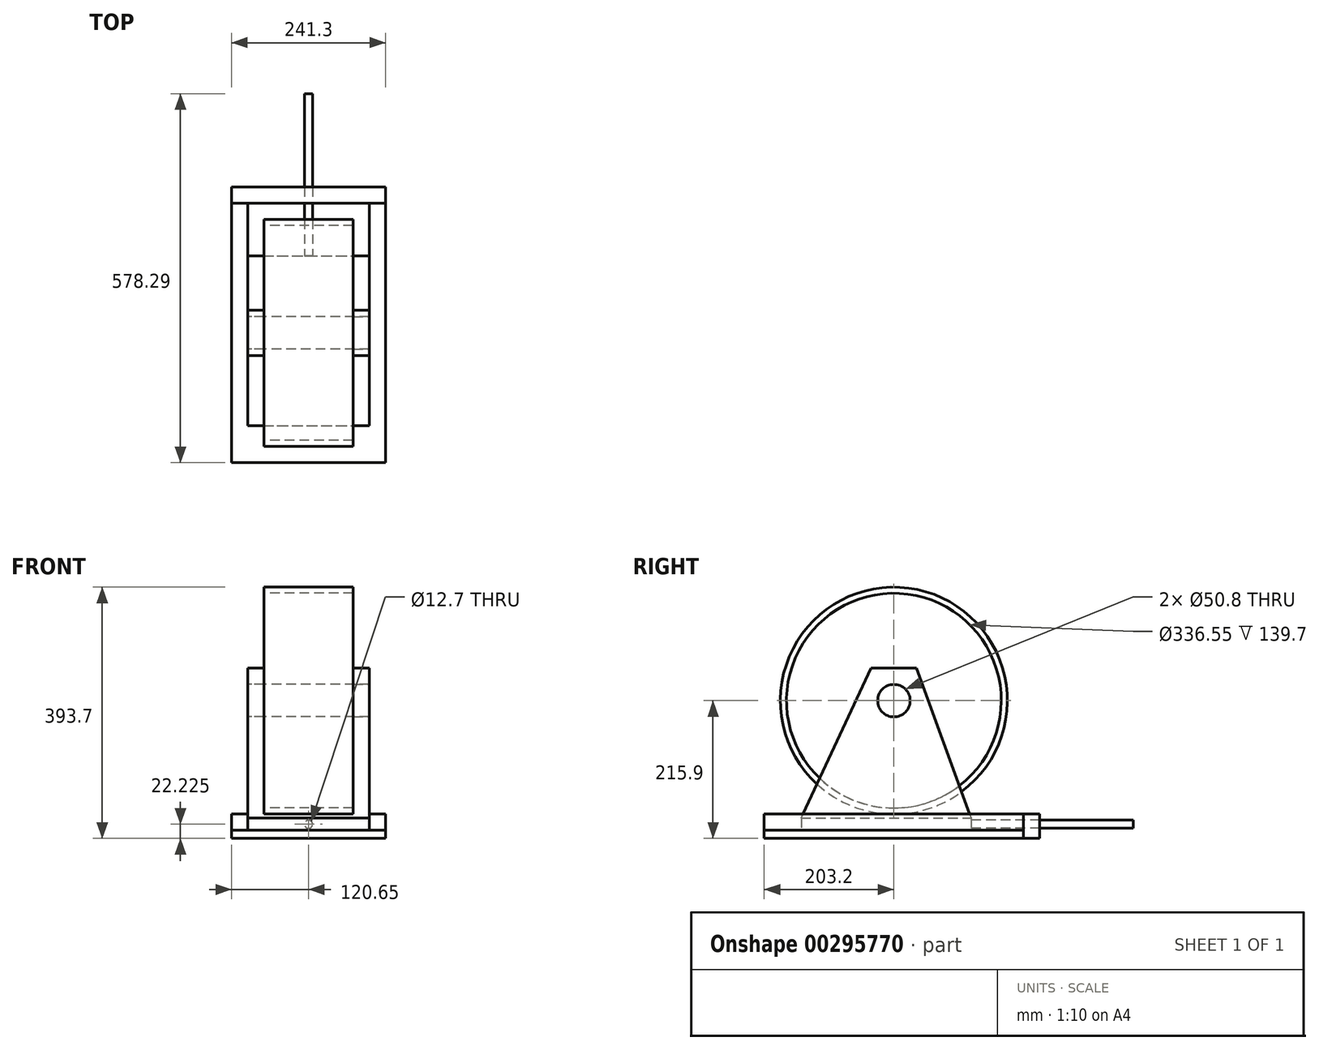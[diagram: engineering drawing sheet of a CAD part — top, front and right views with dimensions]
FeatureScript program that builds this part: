
annotation { "Feature Type Name" : "Feature", "Feature Type Description" : "" }
export const myFeature = defineFeature(function(context is Context, id is Id, definition is map)
    precondition{}
    {
        {
            assignVariable(context, id + "F0", {"name" : "shell_depth", "anyValue" : 139.7 * mm});
        }
        {
            assignVariable(context, id + "F1", {"name" : "stand_side_th", "anyValue" : 25.4 * mm});
        }
        {
            assignVariable(context, id + "F2", {"name" : "shell_rotor_len", "anyValue" : getVariable(context, 'shell_depth') + 2 * getVariable(context, 'stand_side_th')});
        }
        {
            assignVariable(context, id + "F3", {"name" : "rail_th", "anyValue" : 25.4 * mm});
        }
        {
            var Q0;
            Q0=qCreatedBy(makeId("Right.planeOp"),FACE);
            var sketch = newSketch(context, id + "F4", { "sketchPlane" : qUnion([Q0])});
            skCircle(sketch, "E0", {"center": v(0, 203.2) * mm, "radius": 177.8 * mm});
            skCircle(sketch, "E1", {"center": v(0, 203.2) * mm, "radius": 168.28 * mm});
            skCircle(sketch, "E2", {"center": v(0, 203.2) * mm, "radius": 25.4 * mm});
            skSolve(sketch);
        }
        {
            var Q0;
            Q0=makeQuery(id+"F4.imprint","IMPRINT",FACE,{"disambiguationData":[TD([[makeQuery(id+"F4.imprint","IMPRINT",EDGE,{"derivedFrom":sQuery(id+"F4.wireOp",EDGE,"E0")}),1.0]])]});
            extrude(context, id + "F5", {"entities" : qUnion([Q0]), "depth" : getVariable(context, 'shell_depth') / 2, "hasSecondDirection" : true, "secondDirectionOppositeDirection" : true, "secondDirectionDepth" : getVariable(context, 'shell_depth') / 2});
        }
        {
            var Q0;
            Q0=qCreatedBy(makeId("Top.planeOp"),FACE);
            var sketch = newSketch(context, id + "F6", { "sketchPlane" : qUnion([Q0])});
            skLineSegment(sketch, "E3.bottom", {"start": v(-120.65, 203.2) * mm, "end": v(120.65, 203.2) * mm});
            skLineSegment(sketch, "E3.top", {"start": v(-120.65, -203.2) * mm, "end": v(120.65, -203.2) * mm});
            skLineSegment(sketch, "E3.left", {"start": v(-120.65, 203.2) * mm, "end": v(-120.65, -203.2) * mm});
            skLineSegment(sketch, "E3.right", {"start": v(120.65, 203.2) * mm, "end": v(120.65, -203.2) * mm});
            skSolve(sketch);
        }
        {
            var Q0;
            Q0=makeQuery(id+"F6.imprint","IMPRINT",FACE,{"disambiguationData":[TD([[makeQuery(id+"F6.imprint","IMPRINT",EDGE,{"derivedFrom":sQuery(id+"F6.wireOp",EDGE,"E3.bottom")}),-1.0]])]});
            extrude(context, id + "F7", {"entities" : qUnion([Q0]), "oppositeDirection" : true, "depth" : 12.7 * mm});
        }
        {
            var Q0;
            Q0=makeQuery(id+"F4.imprint","IMPRINT",FACE,{"disambiguationData":[TD([[makeQuery(id+"F4.imprint","IMPRINT",EDGE,{"derivedFrom":sQuery(id+"F4.wireOp",EDGE,"E2")}),1.0]])]});
            extrude(context, id + "F8", {"entities" : qUnion([Q0]), "depth" : getVariable(context, 'shell_rotor_len') / 2, "hasSecondDirection" : true, "secondDirectionOppositeDirection" : true, "secondDirectionDepth" : getVariable(context, 'shell_rotor_len') / 2});
        }
        {
            var Q0;
            Q0=makeQuery(id+"F8.opExtrude","CAP_FACE",FACE,{"disambiguationData":[OSD([sQuery(id+"F4.wireOp",EDGE,"E2")])],"isStart":false});
            var sketch = newSketch(context, id + "F9", { "sketchPlane" : qUnion([Q0])});
            skCircle(sketch, "E4.0", {"center": v(0, 203.2) * mm, "radius": 25.4 * mm});
            skLineSegment(sketch, "E5.0", {"start": v(203.2, 0) * mm, "end": v(-203.2, 0) * mm, "construction": true});
            skLineSegment(sketch, "E6.bottom", {"start": v(-145.13, 19.05) * mm, "end": v(121.09, 19.05) * mm});
            skLineSegment(sketch, "E6.top", {"start": v(-145.13, 0) * mm, "end": v(121.09, 0) * mm});
            skLineSegment(sketch, "E6.left", {"start": v(-145.13, 19.05) * mm, "end": v(-145.13, 0) * mm});
            skLineSegment(sketch, "E6.right", {"start": v(121.09, 19.05) * mm, "end": v(121.09, 0) * mm});
            skPoint(sketch, "E7.0", {"position": v(0, 0) * mm});
            skLineSegment(sketch, "E8", {"start": v(-145.13, 19.05) * mm, "end": v(-35.57, 254) * mm});
            skLineSegment(sketch, "E9", {"start": v(-35.57, 254) * mm, "end": v(35.57, 254) * mm});
            skLineSegment(sketch, "E10", {"start": v(35.57, 254) * mm, "end": v(121.09, 19.05) * mm});
            skPoint(sketch, "E11", {"position": v(0, 254) * mm});
            skSolve(sketch);
        }
        {
            var Q0;
            Q0=makeQuery(id+"F9.imprint","IMPRINT",FACE,{"disambiguationData":[TD([[makeQuery(id+"F9.imprint","IMPRINT",EDGE,{"derivedFrom":sQuery(id+"F9.wireOp",EDGE,"E6.bottom")}),-1.0]])]});
            var Q1;
            Q1=makeQuery(id+"F9.imprint","IMPRINT",FACE,{"disambiguationData":[TD([[makeQuery(id+"F9.imprint","IMPRINT",EDGE,{"derivedFrom":sQuery(id+"F9.wireOp",EDGE,"E4.0")}),-1.0]])]});
            extrude(context, id + "F10", {"entities" : qUnion([Q0, Q1]), "oppositeDirection" : true, "depth" : getVariable(context, 'stand_side_th')});
        }
        {
            var Q0;
            Q0=makeQuery(id+"F10.opExtrude","SWEPT_BODY",BODY,{"disambiguationData":[OSD([sQuery(id+"F9.wireOp",EDGE,"E4.0"),sQuery(id+"F9.wireOp",EDGE,"E6.top"),sQuery(id+"F9.wireOp",EDGE,"E6.left"),sQuery(id+"F9.wireOp",EDGE,"E6.right"),sQuery(id+"F9.wireOp",EDGE,"E8"),sQuery(id+"F9.wireOp",EDGE,"E9"),sQuery(id+"F9.wireOp",EDGE,"E10")])]});
            var Q1;
            Q1=makeQuery(id+"F4.imprint","IMPRINT",FACE,{"disambiguationData":[TD([[makeQuery(id+"F4.imprint","IMPRINT",EDGE,{"derivedFrom":sQuery(id+"F4.wireOp",EDGE,"E0")}),1.0]])]});
            mirror(context, id + "F11", {"entities" : qUnion([Q0]), "mirrorPlane" : qUnion([Q1])});
        }
        {
            var Q0;
            Q0=makeQuery(id+"F9.imprint","IMPRINT",FACE,{"disambiguationData":[TD([[makeQuery(id+"F9.imprint","IMPRINT",EDGE,{"derivedFrom":sQuery(id+"F9.wireOp",EDGE,"E6.bottom")}),-1.0]])]});
            extrude(context, id + "F12", {"entities" : qUnion([Q0]), "operationType" : NewBodyOperationType.ADD, "oppositeDirection" : true, "depth" : getVariable(context, 'shell_rotor_len')});
        }
        {
            var Q0;
            Q0=makeQuery(id+"F9.imprint","IMPRINT",FACE,{"disambiguationData":[TD([[makeQuery(id+"F9.imprint","IMPRINT",EDGE,{"derivedFrom":sQuery(id+"F9.wireOp",EDGE,"E4.0")}),-1.0]])]});
            var sketch = newSketch(context, id + "F13", { "sketchPlane" : qUnion([Q0])});
            skLineSegment(sketch, "E12.bottom", {"start": v(-203.2, 25.4) * mm, "end": v(203.2, 25.4) * mm});
            skLineSegment(sketch, "E12.top", {"start": v(-203.2, 0) * mm, "end": v(203.2, 0) * mm});
            skLineSegment(sketch, "E12.left", {"start": v(-203.2, 25.4) * mm, "end": v(-203.2, 0) * mm});
            skLineSegment(sketch, "E12.right", {"start": v(203.2, 25.4) * mm, "end": v(203.2, 0) * mm});
            skLineSegment(sketch, "E13.0", {"start": v(203.2, 0) * mm, "end": v(-203.2, 0) * mm, "construction": true});
            skSolve(sketch);
        }
        {
            var Q0;
            Q0 = qSketchRegion(id + "F13", true);
            extrude(context, id + "F14", {"entities" : qUnion([Q0]), "depth" : getVariable(context, 'rail_th')});
        }
        {
            var Q0;
            Q0=makeQuery(id+"F14.opExtrude","SWEPT_BODY",BODY,{"disambiguationData":[OSD([sQuery(id+"F13.wireOp",EDGE,"E12.bottom"),sQuery(id+"F13.wireOp",EDGE,"E12.top"),sQuery(id+"F13.wireOp",EDGE,"E12.left"),sQuery(id+"F13.wireOp",EDGE,"E12.right")])]});
            var Q1;
            Q1=makeQuery(id+"F4.imprint","IMPRINT",FACE,{"disambiguationData":[TD([[makeQuery(id+"F4.imprint","IMPRINT",EDGE,{"derivedFrom":sQuery(id+"F4.wireOp",EDGE,"E0")}),1.0]])]});
            mirror(context, id + "F15", {"entities" : qUnion([Q0]), "mirrorPlane" : qUnion([Q1])});
        }
        {
            var Q0;
            {var subQ0=sQuery(id+"F9.wireOp",EDGE,"E6.right");var subQ1=makeQuery(id+"F10.opExtrude","SWEPT_FACE",FACE,{"disambiguationData":[OSD([subQ0])]});Q0=makeQuery(id+"F12.boolean.opBoolean","MERGE",FACE,{"derivedFrom":[subQ1,makeQuery(id+"F11.opPattern","COPY",FACE,{"derivedFrom":subQ1,"instanceName":"1"}),makeQuery(id+"F12.opExtrude","SWEPT_FACE",FACE,{"disambiguationData":[OSD([subQ0])]})]});}
            var sketch = newSketch(context, id + "F16", { "sketchPlane" : qUnion([Q0])});
            skLineSegment(sketch, "E14.0", {"start": v(69.85, 19.05) * mm, "end": v(-69.85, 19.05) * mm, "construction": true});
            skLineSegment(sketch, "E15.0", {"start": v(95.25, 0) * mm, "end": v(-95.25, 0) * mm, "construction": true});
            skPoint(sketch, "E16", {"position": v(0, 19.05) * mm});
            skPoint(sketch, "E17", {"position": v(0, 0) * mm});
            skCircle(sketch, "E18", {"center": v(0, 9.52) * mm, "radius": 6.35 * mm});
            skSolve(sketch);
        }
        {
            var Q0;
            Q0=makeQuery(id+"F16.imprint","IMPRINT",FACE,{"disambiguationData":[TD([[makeQuery(id+"F16.imprint","IMPRINT",EDGE,{"derivedFrom":sQuery(id+"F16.wireOp",EDGE,"E18")}),1.0]])]});
            extrude(context, id + "F17", {"entities" : qUnion([Q0]), "depth" : 254 * mm});
        }
        {
            var Q0;
            Q0=makeQuery(id+"F7.opExtrude","SWEPT_FACE",FACE,{"disambiguationData":[OSD([sQuery(id+"F6.wireOp",EDGE,"E3.bottom")])]});
            var sketch = newSketch(context, id + "F18", { "sketchPlane" : qUnion([Q0])});
            skPoint(sketch, "E19.0", {"position": v(-120.65, 25.4) * mm});
            skPoint(sketch, "E20.0", {"position": v(-120.65, -12.7) * mm});
            skPoint(sketch, "E21.0", {"position": v(120.65, -12.7) * mm});
            skPoint(sketch, "E22.0", {"position": v(120.65, 25.4) * mm});
            skLineSegment(sketch, "E23.bottom", {"start": v(-120.65, 25.4) * mm, "end": v(120.65, 25.4) * mm});
            skLineSegment(sketch, "E23.top", {"start": v(-120.65, -12.7) * mm, "end": v(120.65, -12.7) * mm});
            skLineSegment(sketch, "E23.left", {"start": v(-120.65, 25.4) * mm, "end": v(-120.65, -12.7) * mm});
            skLineSegment(sketch, "E23.right", {"start": v(120.65, 25.4) * mm, "end": v(120.65, -12.7) * mm});
            skSolve(sketch);
        }
        {
            var Q0;
            Q0 = qSketchRegion(id + "F18", true);
            extrude(context, id + "F19", {"entities" : qUnion([Q0]), "depth" : 25.4 * mm});
        }
        {
            var Q0;
            Q0=makeQuery(id+"F17.opExtrude","SWEPT_BODY",BODY,{"disambiguationData":[OSD([sQuery(id+"F16.wireOp",EDGE,"E18")])]});
            var Q1;
            Q1=makeQuery(id+"F19.opExtrude","SWEPT_BODY",BODY,{"disambiguationData":[OSD([sQuery(id+"F18.wireOp",EDGE,"E23.bottom"),sQuery(id+"F18.wireOp",EDGE,"E23.top"),sQuery(id+"F18.wireOp",EDGE,"E23.left"),sQuery(id+"F18.wireOp",EDGE,"E23.right")])]});
            booleanBodies(context, id + "F20", {"operationType" : BooleanOperationType.SUBTRACTION, "tools" : qUnion([Q0]), "targets" : qUnion([Q1]), "keepTools" : true});
        }
    });
